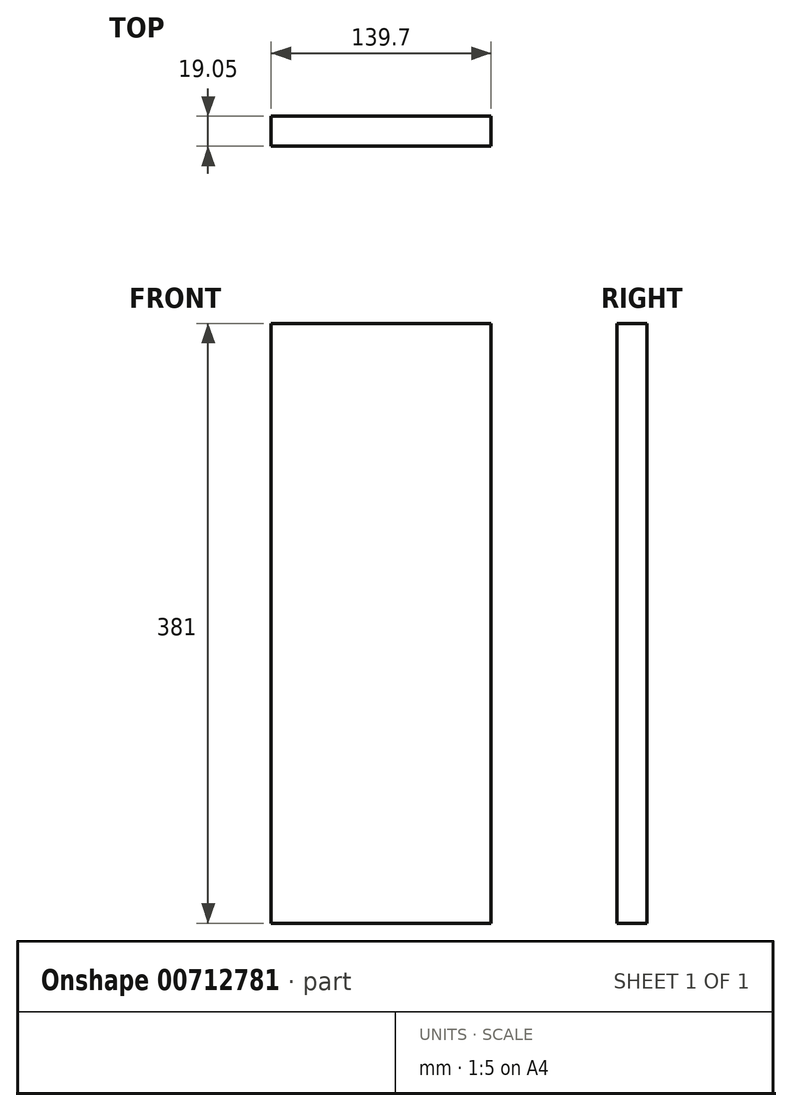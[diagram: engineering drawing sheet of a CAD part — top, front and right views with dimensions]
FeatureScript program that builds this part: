
annotation { "Feature Type Name" : "Feature", "Feature Type Description" : "" }
export const myFeature = defineFeature(function(context is Context, id is Id, definition is map)
    precondition{}
    {
        {
            var Q0;
            Q0=qCreatedBy(makeId("Front.planeOp"),FACE);
            var sketch = newSketch(context, id + "F0", { "sketchPlane" : qUnion([Q0])});
            skLineSegment(sketch, "E0.bottom", {"start": v(-117.56, 373.23) * mm, "end": v(22.14, 373.23) * mm});
            skLineSegment(sketch, "E0.top", {"start": v(-117.56, -7.77) * mm, "end": v(22.14, -7.77) * mm});
            skLineSegment(sketch, "E0.left", {"start": v(-117.56, 373.23) * mm, "end": v(-117.56, -7.77) * mm});
            skLineSegment(sketch, "E0.right", {"start": v(22.14, 373.23) * mm, "end": v(22.14, -7.77) * mm});
            skSolve(sketch);
        }
        {
            var Q0;
            Q0 = qSketchRegion(id + "F0", true);
            extrude(context, id + "F1", {"entities" : qUnion([Q0]), "depth" : 19.05 * mm, "offsetDistance" : 25.4 * mm});
        }
    });
